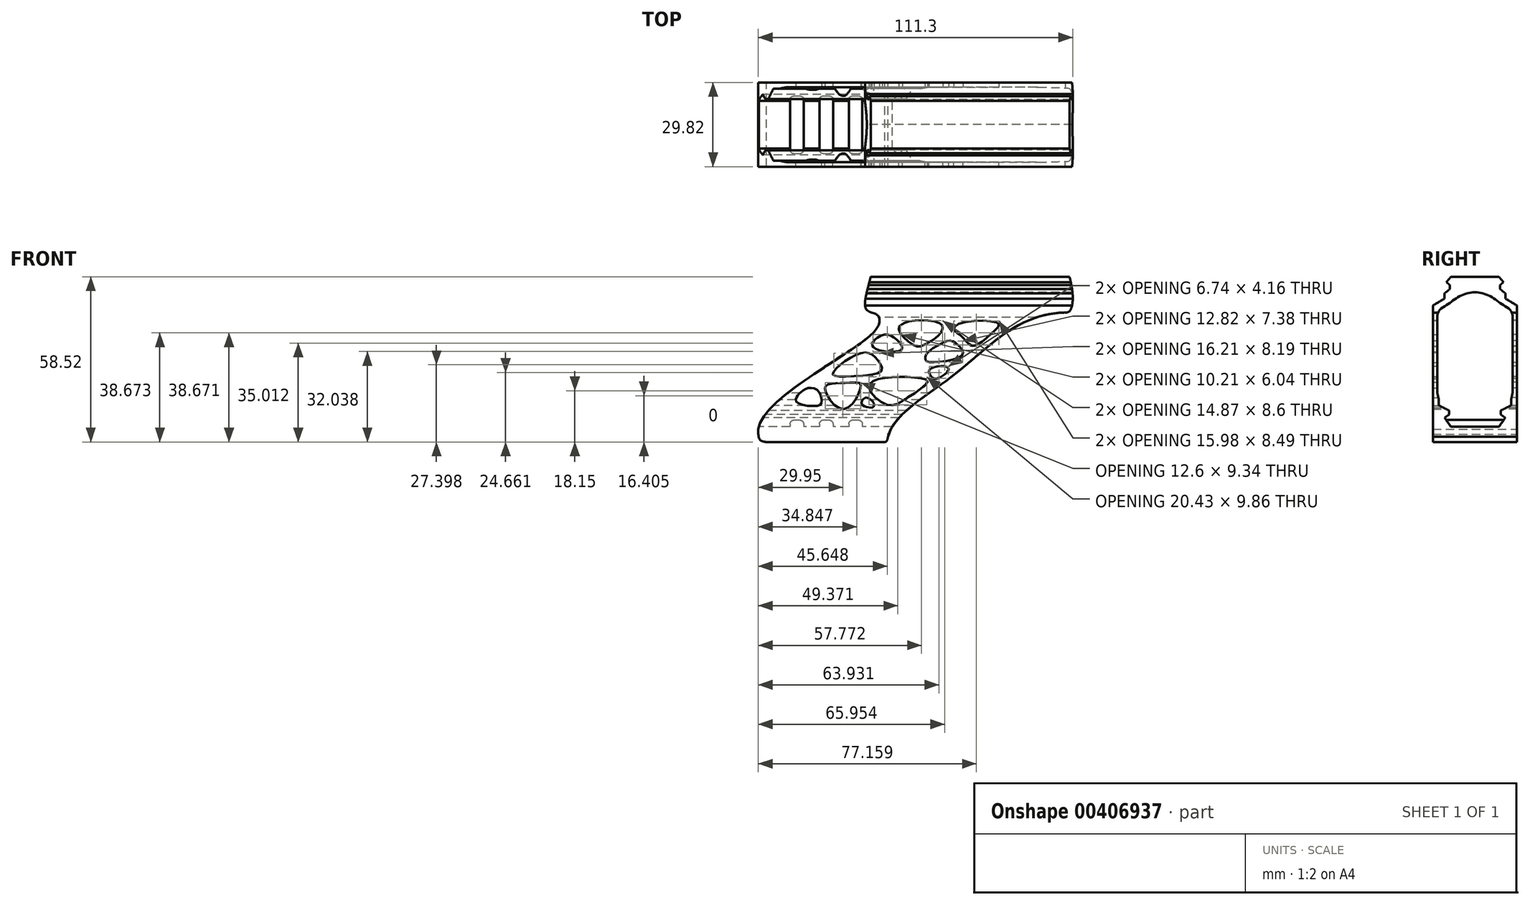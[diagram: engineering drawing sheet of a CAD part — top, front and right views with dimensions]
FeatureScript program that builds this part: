
annotation { "Feature Type Name" : "Feature", "Feature Type Description" : "" }
export const myFeature = defineFeature(function(context is Context, id is Id, definition is map)
    precondition{}
    {
        {
            var Q0;
            Q0=qCreatedBy(makeId("Right.planeOp"),FACE);
            var sketch = newSketch(context, id + "F0", { "sketchPlane" : qUnion([Q0])});
            skLineSegment(sketch, "E0", {"start": v(-8.5, -34.09) * mm, "end": v(-10.6, -31.09) * mm});
            skLineSegment(sketch, "E1", {"start": v(-10.6, -31.09) * mm, "end": v(-9, -29.97) * mm});
            skLineSegment(sketch, "E2", {"start": v(-9, -29.97) * mm, "end": v(-9, -28.47) * mm});
            skLineSegment(sketch, "E3", {"start": v(-9, -28.47) * mm, "end": v(-12.75, -26.59) * mm});
            skLineSegment(sketch, "E4", {"start": v(0, -34.12) * mm, "end": v(0, 4.88) * mm, "construction": true});
            skLineSegment(sketch, "E5", {"start": v(-8.5, -34.09) * mm, "end": v(0, -34.12) * mm});
            skLineSegment(sketch, "E6", {"start": v(-12.75, -26.59) * mm, "end": v(-12.75, 4.88) * mm});
            skLineSegment(sketch, "E7", {"start": v(0, 4.88) * mm, "end": v(-12.75, 4.88) * mm});
            skLineSegment(sketch, "E8.MirrorCS", {"start": v(0, 4.88) * mm, "end": v(12.75, 4.88) * mm});
            skLineSegment(sketch, "E9.MirrorCS", {"start": v(9, -28.47) * mm, "end": v(12.75, -26.59) * mm});
            skLineSegment(sketch, "E10.MirrorCS", {"start": v(9, -29.97) * mm, "end": v(9, -28.47) * mm});
            skLineSegment(sketch, "E11.MirrorCS", {"start": v(10.6, -31.09) * mm, "end": v(9, -29.97) * mm});
            skLineSegment(sketch, "E12.MirrorCS", {"start": v(8.5, -34.09) * mm, "end": v(10.6, -31.09) * mm});
            skLineSegment(sketch, "E13", {"start": v(12.75, 4.88) * mm, "end": v(12.75, -26.59) * mm});
            skLineSegment(sketch, "E14", {"start": v(8.5, -34.09) * mm, "end": v(0, -34.12) * mm});
            skLineSegment(sketch, "E15", {"start": v(-12.75, -26.59) * mm, "end": v(-12.75, -34.09) * mm, "construction": true});
            skLineSegment(sketch, "E16.0", {"start": v(-9.1, -28.53) * mm, "end": v(-12.78, -26.69) * mm});
            skLineSegment(sketch, "E16.1", {"start": v(-9.1, -29.92) * mm, "end": v(-9.1, -28.53) * mm});
            skLineSegment(sketch, "E16.2", {"start": v(-10.73, -31.06) * mm, "end": v(-9.1, -29.92) * mm});
            skLineSegment(sketch, "E17", {"start": v(-10.73, -31.06) * mm, "end": v(-8.5, -34.25) * mm});
            skLineSegment(sketch, "E18", {"start": v(-8.5, -34.25) * mm, "end": v(0, -34.25) * mm});
            skLineSegment(sketch, "E19", {"start": v(-12.78, -26.69) * mm, "end": v(-12.78, -24.69) * mm});
            skLineSegment(sketch, "E20", {"start": v(-12.78, -24.69) * mm, "end": v(-13.32, -22.27) * mm});
            skLineSegment(sketch, "E21", {"start": v(-13.32, -22.27) * mm, "end": v(-13.32, 4.48) * mm});
            skLineSegment(sketch, "E22.bottom", {"start": v(-3.09, 4.88) * mm, "end": v(2.91, 4.88) * mm});
            skLineSegment(sketch, "E22.top", {"start": v(-3.09, 7.88) * mm, "end": v(2.91, 7.88) * mm});
            skLineSegment(sketch, "E22.left", {"start": v(-3.09, 4.88) * mm, "end": v(-3.09, 7.88) * mm});
            skLineSegment(sketch, "E22.right", {"start": v(2.91, 4.88) * mm, "end": v(2.91, 7.88) * mm});
            skFitSpline(sketch, "E23", {"points": [v(-13.32, 4.48) * mm, v(-9.8, 8.96) * mm, v(0, 13.43) * mm], "startDerivative": vector(-0.69, 19.34) * mm, "endDerivative": vector(26.9, 1.58) * mm});
            skLineSegment(sketch, "E24", {"start": v(0, 13.43) * mm, "end": v(0, 18.86) * mm});
            skLineSegment(sketch, "E25", {"start": v(0, 18.86) * mm, "end": v(-8.5, 18.86) * mm});
            skLineSegment(sketch, "E26", {"start": v(-8.5, 18.86) * mm, "end": v(-10.1, 16.99) * mm});
            skLineSegment(sketch, "E27", {"start": v(-10.1, 16.99) * mm, "end": v(-8.94, 15.99) * mm});
            skLineSegment(sketch, "E28", {"start": v(-8.94, 15.99) * mm, "end": v(-8.94, 14.49) * mm});
            skLineSegment(sketch, "E29", {"start": v(-8.94, 14.49) * mm, "end": v(-10.82, 12.96) * mm});
            skLineSegment(sketch, "E30", {"start": v(-10.82, 12.96) * mm, "end": v(-10.82, 11.14) * mm});
            skLineSegment(sketch, "E31", {"start": v(-10.82, 11.14) * mm, "end": v(-14.91, 8.67) * mm});
            skLineSegment(sketch, "E32", {"start": v(-14.91, 8.67) * mm, "end": v(-14.91, -39.66) * mm});
            skLineSegment(sketch, "E33", {"start": v(-14.91, -39.66) * mm, "end": v(0, -39.66) * mm});
            skLineSegment(sketch, "E34", {"start": v(0, -39.66) * mm, "end": v(0, -34.25) * mm});
            skSolve(sketch);
        }
        {
            var Q0;
            Q0=makeQuery(id+"F0.imprint","IMPRINT",FACE,{"disambiguationData":[TD([[makeQuery(id+"F0.imprint","IMPRINT",EDGE,{"derivedFrom":sQuery(id+"F0.wireOp",EDGE,"E16.0")}),1.0]])]});
            extrude(context, id + "F1", {"entities" : qUnion([Q0]), "depth" : 57 * mm, "hasSecondDirection" : true, "secondDirectionOppositeDirection" : true, "secondDirectionDepth" : 55 * mm});
        }
        {
            var Q0;
            Q0=qCreatedBy(makeId("Front.planeOp"),FACE);
            var sketch = newSketch(context, id + "F2", { "sketchPlane" : qUnion([Q0])});
            skFitSpline(sketch, "E35", {"points": [v(53.66, 6.22) * mm, v(34.13, 0) * mm, v(11.58, -17.9) * mm, v(-9.08, -37.73) * mm], "startDerivative": vector(-71.87, -1.54) * mm, "endDerivative": vector(-15.43, -64.12) * mm});
            skFitSpline(sketch, "E36", {"points": [v(-55.02, -35.65) * mm, v(-21.25, -6.37) * mm, v(-12.1, 2.87) * mm, v(-15.2, 6.28) * mm], "startDerivative": vector(0, 49.33) * mm, "endDerivative": vector(-48.35, 7.6) * mm});
            skFitSpline(sketch, "E37", {"points": [v(-15.02, 19.66) * mm, v(-17.06, 7.88) * mm, v(-15.2, 6.28) * mm], "startDerivative": vector(-4.96, -21) * mm, "endDerivative": vector(6.53, -2.72) * mm});
            skFitSpline(sketch, "E38", {"points": [v(54.98, 19.66) * mm, v(56.14, 9.16) * mm, v(53.66, 6.22) * mm], "startDerivative": vector(5.75, -21.75) * mm, "endDerivative": vector(-13.53, 1.34) * mm});
            skFitSpline(sketch, "E39", {"points": [v(-55.02, -35.65) * mm, v(-51.61, -39.72) * mm, v(-11.2, -39.72) * mm, v(-9.08, -37.73) * mm], "startDerivative": vector(-0.45, -45) * mm, "endDerivative": vector(7.03, 35.86) * mm});
            skLineSegment(sketch, "E40", {"start": v(-15.02, 19.66) * mm, "end": v(54.98, 19.66) * mm});
            skFitSpline(sketch, "E41", {"points": [v(4.54, -8.4) * mm, v(9.2, -5.08) * mm, v(12.44, -3.75) * mm, v(15.57, -5.16) * mm, v(17.38, -8.7) * mm, v(8.1, -11.36) * mm, v(4.28, -10.79) * mm, v(4.54, -8.4) * mm]});
            skFitSpline(sketch, "E42", {"points": [v(-12.5, -17.38) * mm, v(0, -16.77) * mm, v(4.86, -18.29) * mm, v(-2.81, -24.34) * mm, v(-9.37, -26.46) * mm, v(-15.84, -20.3) * mm, v(-12.5, -17.38) * mm]});
            skFitSpline(sketch, "E43", {"points": [v(-18.75, -8.17) * mm, v(-14.98, -8.6) * mm, v(-12.35, -11.21) * mm, v(-11.36, -14.42) * mm, v(-24.54, -16.42) * mm, v(-28.67, -15.7) * mm, v(-26.3, -12.6) * mm, v(-18.75, -8.17) * mm]});
            skFitSpline(sketch, "E44", {"points": [v(-18.75, -19.4) * mm, v(-21.19, -18.59) * mm, v(-29.37, -19.1) * mm, v(-31.38, -20.7) * mm, v(-24.7, -27.99) * mm, v(-18.75, -19.4) * mm]});
            skFitSpline(sketch, "E45", {"points": [v(-18.05, -26.65) * mm, v(-18.3, -25.12) * mm, v(-17.1, -23.97) * mm, v(-15.42, -24.48) * mm, v(-14.17, -25.84) * mm, v(-14.33, -27.23) * mm, v(-18.05, -26.65) * mm]});
            skFitSpline(sketch, "E46", {"points": [v(-41.5, -23.87) * mm, v(-40.05, -22.13) * mm, v(-37.48, -20.56) * mm, v(-33.8, -21.52) * mm, v(-32.59, -25.09) * mm, v(-33.45, -26.65) * mm, v(-41.24, -25.69) * mm, v(-41.5, -23.87) * mm]});
            skFitSpline(sketch, "E47", {"points": [v(16.37, -1.63) * mm, v(14.25, 0) * mm, v(15.8, 2.16) * mm, v(29.96, 2.42) * mm, v(28.81, 0) * mm, v(22.33, -5.26) * mm, v(19.8, -5.16) * mm, v(16.37, -1.63) * mm]});
            skFitSpline(sketch, "E48", {"points": [v(3.67, -5.25) * mm, v(9.7, -0.82) * mm, v(9.74, 2.07) * mm, v(0.95, 3.39) * mm, v(-4.5, 1.9) * mm, v(-5.23, 0) * mm, v(0, -5.37) * mm, v(3.67, -5.25) * mm]});
            skFitSpline(sketch, "E49", {"points": [v(-10.38, -1.63) * mm, v(-14.73, -5.26) * mm, v(-9.4, -7.61) * mm, v(-4.16, -6.7) * mm, v(-5.34, -4.05) * mm, v(-10.38, -1.63) * mm]});
            skFitSpline(sketch, "E50", {"points": [v(5.75, -15.83) * mm, v(5.76, -13.83) * mm, v(11.63, -13.02) * mm, v(12.23, -14.36) * mm, v(9.07, -16.89) * mm, v(7.23, -17.12) * mm, v(5.75, -15.83) * mm]});
            skSolve(sketch);
        }
        {
            var Q0;
            Q0=qCreatedBy(makeId("Front.planeOp"),FACE);
            var sketch = newSketch(context, id + "F3", { "sketchPlane" : qUnion([Q0])});
            skLineSegment(sketch, "E51.bottom", {"start": v(-54.96, -39.74) * mm, "end": v(34.89, -39.74) * mm});
            skLineSegment(sketch, "E51.top", {"start": v(-54.96, -11.12) * mm, "end": v(34.89, -11.12) * mm});
            skLineSegment(sketch, "E51.left", {"start": v(-54.96, -39.74) * mm, "end": v(-54.96, -11.12) * mm});
            skLineSegment(sketch, "E51.right", {"start": v(34.89, -39.74) * mm, "end": v(34.89, -11.12) * mm});
            skLineSegment(sketch, "E52.bottom", {"start": v(-22.96, -31.85) * mm, "end": v(-18.16, -31.85) * mm});
            skLineSegment(sketch, "E52.top", {"start": v(-22.96, -34.75) * mm, "end": v(-18.16, -34.75) * mm});
            skLineSegment(sketch, "E52.left", {"start": v(-22.96, -31.85) * mm, "end": v(-22.96, -34.75) * mm});
            skLineSegment(sketch, "E52.right", {"start": v(-18.16, -31.85) * mm, "end": v(-18.16, -34.75) * mm});
            skLineSegment(sketch, "E53.1.0.0", {"start": v(-33.36, -31.85) * mm, "end": v(-33.36, -34.75) * mm});
            skLineSegment(sketch, "E53.1.0.1", {"start": v(-33.36, -31.85) * mm, "end": v(-28.56, -31.85) * mm});
            skLineSegment(sketch, "E53.1.0.2", {"start": v(-33.36, -34.75) * mm, "end": v(-28.56, -34.75) * mm});
            skLineSegment(sketch, "E53.1.0.3", {"start": v(-28.56, -31.85) * mm, "end": v(-28.56, -34.75) * mm});
            skLineSegment(sketch, "E53.2.0.0", {"start": v(-43.76, -31.85) * mm, "end": v(-43.76, -34.75) * mm});
            skLineSegment(sketch, "E53.2.0.1", {"start": v(-43.76, -31.85) * mm, "end": v(-38.96, -31.85) * mm});
            skLineSegment(sketch, "E53.2.0.2", {"start": v(-43.76, -34.75) * mm, "end": v(-38.96, -34.75) * mm});
            skLineSegment(sketch, "E53.2.0.3", {"start": v(-38.96, -31.85) * mm, "end": v(-38.96, -34.75) * mm});
            skLineSegment(sketch, "E53.direction1", {"start": v(-22.96, -34.75) * mm, "end": v(-33.36, -34.75) * mm, "construction": true});
            skPoint(sketch, "E54", {"position": v(-20.56, -34.01) * mm});
            skPoint(sketch, "E55", {"position": v(-30.96, -34.01) * mm});
            skPoint(sketch, "E56", {"position": v(-41.36, -34.01) * mm});
            skSolve(sketch);
        }
        {
            var Q0;
            Q0=makeQuery(id+"F3.imprint","IMPRINT",FACE,{"disambiguationData":[TD([[makeQuery(id+"F3.imprint","IMPRINT",EDGE,{"derivedFrom":sQuery(id+"F3.wireOp",EDGE,"E53.2.0.0")}),1.0]])]});
            var Q1;
            Q1=makeQuery(id+"F3.imprint","IMPRINT",FACE,{"disambiguationData":[TD([[makeQuery(id+"F3.imprint","IMPRINT",EDGE,{"derivedFrom":sQuery(id+"F3.wireOp",EDGE,"E52.bottom")}),-1.0]])]});
            var Q2;
            Q2=makeQuery(id+"F3.imprint","IMPRINT",FACE,{"disambiguationData":[TD([[makeQuery(id+"F3.imprint","IMPRINT",EDGE,{"derivedFrom":sQuery(id+"F3.wireOp",EDGE,"E53.1.0.0")}),1.0]])]});
            extrude(context, id + "F4", {"entities" : qUnion([Q0, Q1, Q2]), "operationType" : NewBodyOperationType.ADD, "depth" : 14.1 * mm});
        }
        {
            var Q0;
            Q0=makeQuery(id+"F4.opExtrude","SWEPT_EDGE",EDGE,{"disambiguationData":[OSD([sQuery(id+"F3.wireOp",EDGE,"E52.bottom"),sQuery(id+"F3.wireOp",EDGE,"E52.right")])]});
            var Q1;
            Q1=makeQuery(id+"F4.opExtrude","SWEPT_EDGE",EDGE,{"disambiguationData":[OSD([sQuery(id+"F3.wireOp",EDGE,"E52.bottom"),sQuery(id+"F3.wireOp",EDGE,"E52.left")])]});
            var Q2;
            Q2=makeQuery(id+"F4.opExtrude","SWEPT_EDGE",EDGE,{"disambiguationData":[OSD([sQuery(id+"F3.wireOp",EDGE,"E53.1.0.1"),sQuery(id+"F3.wireOp",EDGE,"E53.1.0.3")])]});
            var Q3;
            Q3=makeQuery(id+"F4.opExtrude","SWEPT_EDGE",EDGE,{"disambiguationData":[OSD([sQuery(id+"F3.wireOp",EDGE,"E53.1.0.0"),sQuery(id+"F3.wireOp",EDGE,"E53.1.0.1")])]});
            var Q4;
            Q4=makeQuery(id+"F4.opExtrude","SWEPT_EDGE",EDGE,{"disambiguationData":[OSD([sQuery(id+"F3.wireOp",EDGE,"E53.2.0.1"),sQuery(id+"F3.wireOp",EDGE,"E53.2.0.3")])]});
            var Q5;
            Q5=makeQuery(id+"F4.opExtrude","SWEPT_EDGE",EDGE,{"disambiguationData":[OSD([sQuery(id+"F3.wireOp",EDGE,"E53.2.0.0"),sQuery(id+"F3.wireOp",EDGE,"E53.2.0.1")])]});
            fillet(context, id + "F5", {"entities" : qUnion([Q0, Q1, Q2, Q3, Q4, Q5]), "radius" : 1.5 * mm, "tangentPropagation" : true, "allowEdgeOverflow" : false});
        }
        {
            var Q0;
            Q0=qSketchRegion(id+"F2",true);
            extrude(context, id + "F6", {"entities" : qUnion([Q0]), "operationType" : NewBodyOperationType.INTERSECT, "depth" : 25 * mm});
        }
        {
            var Q0;
            Q0=makeQuery(id+"F1.opExtrude","SWEPT_BODY",BODY,{"disambiguationData":[OSD([sQuery(id+"F0.wireOp",EDGE,"E16.0"),sQuery(id+"F0.wireOp",EDGE,"E16.1"),sQuery(id+"F0.wireOp",EDGE,"E16.2"),sQuery(id+"F0.wireOp",EDGE,"E17"),sQuery(id+"F0.wireOp",EDGE,"E18"),sQuery(id+"F0.wireOp",EDGE,"E19"),sQuery(id+"F0.wireOp",EDGE,"E20"),sQuery(id+"F0.wireOp",EDGE,"E21"),sQuery(id+"F0.wireOp",EDGE,"E23"),sQuery(id+"F0.wireOp",EDGE,"E24"),sQuery(id+"F0.wireOp",EDGE,"E25"),sQuery(id+"F0.wireOp",EDGE,"E26"),sQuery(id+"F0.wireOp",EDGE,"E27"),sQuery(id+"F0.wireOp",EDGE,"E28"),sQuery(id+"F0.wireOp",EDGE,"E29"),sQuery(id+"F0.wireOp",EDGE,"E30"),sQuery(id+"F0.wireOp",EDGE,"E31"),sQuery(id+"F0.wireOp",EDGE,"E32"),sQuery(id+"F0.wireOp",EDGE,"E33"),sQuery(id+"F0.wireOp",EDGE,"E34")])]});
            var Q1;
            Q1=qCreatedBy(makeId("Front.planeOp"),FACE);
            mirror(context, id + "F7", {"operationType" : NewBodyOperationType.ADD, "entities" : qUnion([Q0]), "mirrorPlane" : qUnion([Q1])});
        }
    });
